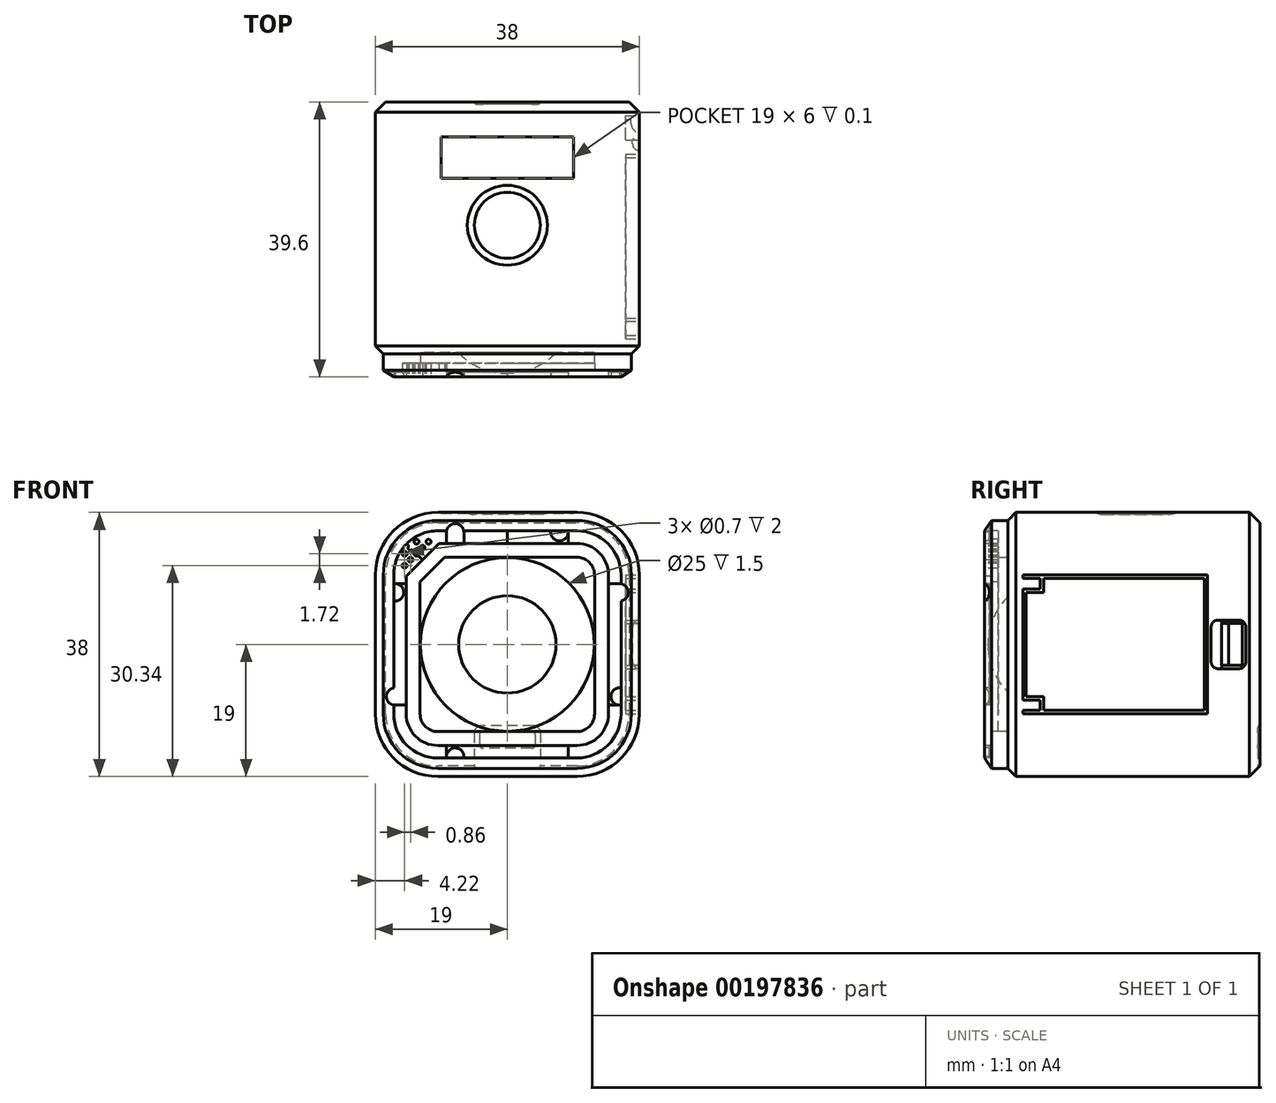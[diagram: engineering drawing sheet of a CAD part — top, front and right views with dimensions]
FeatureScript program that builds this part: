
annotation { "Feature Type Name" : "Feature", "Feature Type Description" : "" }
export const myFeature = defineFeature(function(context is Context, id is Id, definition is map)
    precondition{}
    {
        {
            var Q0;
            Q0=qCreatedBy(makeId("Front.planeOp"),FACE);
            var sketch = newSketch(context, id + "F0", { "sketchPlane" : qUnion([Q0])});
            skLineSegment(sketch, "E0.bottom", {"start": v(19, 19) * mm, "end": v(-19, 19) * mm});
            skLineSegment(sketch, "E0.top", {"start": v(19, -19) * mm, "end": v(-19, -19) * mm});
            skLineSegment(sketch, "E0.left", {"start": v(19, 19) * mm, "end": v(19, -19) * mm});
            skLineSegment(sketch, "E0.right", {"start": v(-19, 19) * mm, "end": v(-19, -19) * mm});
            skPoint(sketch, "E0.middle", {"position": v(0, 0) * mm});
            skLineSegment(sketch, "E1.0", {"start": v(17.85, 17.85) * mm, "end": v(-17.85, 17.85) * mm});
            skLineSegment(sketch, "E1.1", {"start": v(17.85, 17.85) * mm, "end": v(17.85, -17.85) * mm});
            skLineSegment(sketch, "E1.2", {"start": v(17.85, -17.85) * mm, "end": v(-17.85, -17.85) * mm});
            skLineSegment(sketch, "E1.3", {"start": v(-17.85, 17.85) * mm, "end": v(-17.85, -17.85) * mm});
            skSolve(sketch);
        }
        {
            var Q0;
            Q0=makeQuery(id+"F0.imprint","IMPRINT",FACE,{"disambiguationData":[TD([[makeQuery(id+"F0.imprint","IMPRINT",EDGE,{"derivedFrom":sQuery(id+"F0.wireOp",EDGE,"E0.bottom")}),1.0]])]});
            var Q1;
            Q1=makeQuery(id+"F0.imprint","IMPRINT",FACE,{"disambiguationData":[TD([[makeQuery(id+"F0.imprint","IMPRINT",EDGE,{"derivedFrom":sQuery(id+"F0.wireOp",EDGE,"E1.0")}),1.0]])]});
            extrude(context, id + "F1", {"entities" : qUnion([Q0, Q1]), "oppositeDirection" : true, "depth" : 36.6 * mm});
        }
        {
            var Q0;
            Q0=makeQuery(id+"F1.opExtrude","SWEPT_EDGE",EDGE,{"disambiguationData":[OSD([sQuery(id+"F0.wireOp",EDGE,"E0.bottom"),sQuery(id+"F0.wireOp",EDGE,"E0.left")])]});
            var Q1;
            Q1=makeQuery(id+"F1.opExtrude","SWEPT_EDGE",EDGE,{"disambiguationData":[OSD([sQuery(id+"F0.wireOp",EDGE,"E0.bottom"),sQuery(id+"F0.wireOp",EDGE,"E0.right")])]});
            var Q2;
            Q2=makeQuery(id+"F1.opExtrude","SWEPT_EDGE",EDGE,{"disambiguationData":[OSD([sQuery(id+"F0.wireOp",EDGE,"E0.top"),sQuery(id+"F0.wireOp",EDGE,"E0.left")])]});
            var Q3;
            Q3=makeQuery(id+"F1.opExtrude","SWEPT_EDGE",EDGE,{"disambiguationData":[OSD([sQuery(id+"F0.wireOp",EDGE,"E0.top"),sQuery(id+"F0.wireOp",EDGE,"E0.right")])]});
            fillet(context, id + "F2", {"entities" : qUnion([Q0, Q1, Q2, Q3]), "radius" : 9 * mm, "tangentPropagation" : true, "allowEdgeOverflow" : false});
        }
        {
            var Q0;
            Q0=makeQuery(id+"F0.imprint","IMPRINT",FACE,{"disambiguationData":[TD([[makeQuery(id+"F0.imprint","IMPRINT",EDGE,{"derivedFrom":sQuery(id+"F0.wireOp",EDGE,"E1.0")}),1.0]])]});
            extrude(context, id + "F3", {"entities" : qUnion([Q0]), "operationType" : NewBodyOperationType.ADD, "depth" : 3 * mm});
        }
        {
            var Q0;
            Q0=makeQuery(id+"F3.opExtrude","SWEPT_EDGE",EDGE,{"disambiguationData":[OSD([sQuery(id+"F0.wireOp",EDGE,"E1.0"),sQuery(id+"F0.wireOp",EDGE,"E1.1")])]});
            var Q1;
            Q1=makeQuery(id+"F3.opExtrude","SWEPT_EDGE",EDGE,{"disambiguationData":[OSD([sQuery(id+"F0.wireOp",EDGE,"E1.0"),sQuery(id+"F0.wireOp",EDGE,"E1.3")])]});
            var Q2;
            Q2=makeQuery(id+"F3.opExtrude","SWEPT_EDGE",EDGE,{"disambiguationData":[OSD([sQuery(id+"F0.wireOp",EDGE,"E1.2"),sQuery(id+"F0.wireOp",EDGE,"E1.3")])]});
            var Q3;
            Q3=makeQuery(id+"F3.opExtrude","SWEPT_EDGE",EDGE,{"disambiguationData":[OSD([sQuery(id+"F0.wireOp",EDGE,"E1.1"),sQuery(id+"F0.wireOp",EDGE,"E1.2")])]});
            fillet(context, id + "F4", {"entities" : qUnion([Q0, Q1, Q2, Q3]), "radius" : 7.85 * mm, "tangentPropagation" : true, "allowEdgeOverflow" : false});
        }
        {
            var Q0;
            Q0=makeQuery(id+"F1.opExtrude","SWEPT_FACE",FACE,{"disambiguationData":[OSD([sQuery(id+"F0.wireOp",EDGE,"E0.bottom")])]});
            var sketch = newSketch(context, id + "F5", { "sketchPlane" : qUnion([Q0])});
            skCircle(sketch, "E2", {"center": v(0, 18.85) * mm, "radius": 5.75 * mm});
            skCircle(sketch, "E3.0", {"center": v(0, 18.85) * mm, "radius": 4.75 * mm});
            skLineSegment(sketch, "E4.bottom", {"start": v(-9.5, 31.6) * mm, "end": v(9.5, 31.6) * mm});
            skLineSegment(sketch, "E4.top", {"start": v(-9.5, 25.6) * mm, "end": v(9.5, 25.6) * mm});
            skLineSegment(sketch, "E4.left", {"start": v(-9.5, 31.6) * mm, "end": v(-9.5, 25.6) * mm});
            skLineSegment(sketch, "E4.right", {"start": v(9.5, 31.6) * mm, "end": v(9.5, 25.6) * mm});
            skPoint(sketch, "E4.middle", {"position": v(0, 28.6) * mm});
            skSolve(sketch);
        }
        {
            var Q0;
            Q0=makeQuery(id+"F5.imprint","IMPRINT",FACE,{"disambiguationData":[TD([[makeQuery(id+"F5.imprint","IMPRINT",EDGE,{"derivedFrom":sQuery(id+"F5.wireOp",EDGE,"E2")}),1.0]])]});
            extrude(context, id + "F6", {"entities" : qUnion([Q0]), "operationType" : NewBodyOperationType.REMOVE, "oppositeDirection" : true, "depth" : 0.3 * mm});
        }
        {
            var Q0;
            Q0=makeQuery(id+"F6.boolean.opBoolean","COPY",EDGE,{"derivedFrom":makeQuery(id+"F6.opExtrude","CAP_EDGE",EDGE,{"disambiguationData":[OSD([sQuery(id+"F5.wireOp",EDGE,"E3.0")])],"isStart":true})});
            fillet(context, id + "F7", {"entities" : qUnion([Q0]), "radius" : 0.1 * mm, "tangentPropagation" : true, "allowEdgeOverflow" : false});
        }
        {
            var Q0;
            Q0=makeQuery(id+"F5.imprint","IMPRINT",FACE,{"disambiguationData":[TD([[makeQuery(id+"F5.imprint","IMPRINT",EDGE,{"derivedFrom":sQuery(id+"F5.wireOp",EDGE,"E4.bottom")}),-1.0]])]});
            extrude(context, id + "F8", {"entities" : qUnion([Q0]), "operationType" : NewBodyOperationType.REMOVE, "oppositeDirection" : true, "depth" : 0.1 * mm});
        }
        {
            var Q0;
            Q0=makeQuery(id+"F6.boolean.opBoolean","COPY",EDGE,{"derivedFrom":makeQuery(id+"F6.opExtrude","CAP_EDGE",EDGE,{"disambiguationData":[OSD([sQuery(id+"F5.wireOp",EDGE,"E2")])],"isStart":false})});
            fillet(context, id + "F9", {"entities" : qUnion([Q0]), "radius" : 1.7 * mm, "tangentPropagation" : true, "allowEdgeOverflow" : false});
        }
        {
            var Q0;
            Q0=makeQuery(id+"F1.opExtrude","CAP_FACE",FACE,{"disambiguationData":[OSD([sQuery(id+"F0.wireOp",EDGE,"E0.bottom"),sQuery(id+"F0.wireOp",EDGE,"E0.top"),sQuery(id+"F0.wireOp",EDGE,"E0.left"),sQuery(id+"F0.wireOp",EDGE,"E0.right")])],"isStart":false});
            var Q1;
            Q1=makeQuery(id+"F1.opExtrude","CAP_EDGE",EDGE,{"disambiguationData":[OSD([sQuery(id+"F0.wireOp",EDGE,"E0.bottom")])],"isStart":true});
            chamfer(context, id + "F10", {"entities" : qUnion([Q0, Q1]), "width" : 1.5 * mm, "tangentPropagation" : true});
        }
        {
            var Q0;
            Q0=makeQuery(id+"F3.opExtrude","CAP_FACE",FACE,{"disambiguationData":[OSD([sQuery(id+"F0.wireOp",EDGE,"E1.0"),sQuery(id+"F0.wireOp",EDGE,"E1.1"),sQuery(id+"F0.wireOp",EDGE,"E1.2"),sQuery(id+"F0.wireOp",EDGE,"E1.3")])],"isStart":false});
            chamfer(context, id + "F11", {"entities" : qUnion([Q0]), "chamferType" : ChamferType.TWO_OFFSETS, "width1" : 1.5 * mm, "oppositeDirection" : false, "width2" : 1 * mm, "tangentPropagation" : true});
        }
        {
            var Q0;
            Q0=makeQuery(id+"F3.opExtrude","CAP_FACE",FACE,{"disambiguationData":[OSD([sQuery(id+"F0.wireOp",EDGE,"E1.0"),sQuery(id+"F0.wireOp",EDGE,"E1.1"),sQuery(id+"F0.wireOp",EDGE,"E1.2"),sQuery(id+"F0.wireOp",EDGE,"E1.3")])],"isStart":false});
            var sketch = newSketch(context, id + "F12", { "sketchPlane" : qUnion([Q0])});
            skLineSegment(sketch, "E5.1", {"start": v(10, 14.55) * mm, "end": v(-9.85, 14.55) * mm});
            skLineSegment(sketch, "E5.2", {"start": v(-14.55, 9.85) * mm, "end": v(-14.55, -10) * mm});
            skArc(sketch, "E5.3", {"start": v(14.55, 10) * mm, "mid": v(13.22, 13.22) * mm, "end": v(10, 14.55) * mm});
            skArc(sketch, "E5.4", {"start": v(-14.55, -10) * mm, "mid": v(-13.22, -13.22) * mm, "end": v(-10, -14.55) * mm});
            skLineSegment(sketch, "E5.5", {"start": v(-10, -14.55) * mm, "end": v(10, -14.55) * mm});
            skArc(sketch, "E5.6", {"start": v(10, -14.55) * mm, "mid": v(13.22, -13.22) * mm, "end": v(14.55, -10) * mm});
            skLineSegment(sketch, "E5.7", {"start": v(14.55, -10) * mm, "end": v(14.55, 10) * mm});
            skLineSegment(sketch, "E6", {"start": v(-14.55, 9.85) * mm, "end": v(-9.85, 14.55) * mm});
            skCircle(sketch, "E7", {"center": v(-13.06, 13.06) * mm, "radius": 0.35 * mm});
            skLineSegment(sketch, "E8", {"start": v(-12.2, 12.2) * mm, "end": v(-14.5, 14.5) * mm});
            skCircle(sketch, "E9", {"center": v(-13.92, 13.92) * mm, "radius": 0.35 * mm});
            skCircle(sketch, "E10", {"center": v(-13.92, 12.2) * mm, "radius": 0.35 * mm});
            skCircle(sketch, "E11", {"center": v(-14.78, 11.34) * mm, "radius": 0.35 * mm});
            skCircle(sketch, "E12", {"center": v(-14.78, 13.06) * mm, "radius": 0.35 * mm});
            skCircle(sketch, "E13.MirrorC", {"center": v(-12.2, 13.92) * mm, "radius": 0.35 * mm});
            skCircle(sketch, "E14.MirrorC", {"center": v(-13.06, 14.78) * mm, "radius": 0.35 * mm});
            skCircle(sketch, "E15.MirrorC", {"center": v(-11.34, 14.78) * mm, "radius": 0.35 * mm});
            skPoint(sketch, "E16", {"position": v(-7.5, 16.15) * mm});
            skLineSegment(sketch, "E17", {"start": v(0, 16.35) * mm, "end": v(0, 14.55) * mm});
            skCircle(sketch, "E18", {"center": v(-7.5, 16.15) * mm, "radius": 1.25 * mm});
            skLineSegment(sketch, "E19", {"start": v(-8.75, 16.15) * mm, "end": v(-8.75, 14.55) * mm});
            skLineSegment(sketch, "E20", {"start": v(-6.25, 16.15) * mm, "end": v(-6.25, 14.55) * mm});
            skLineSegment(sketch, "E21.MirrorCS", {"start": v(6.25, 16.15) * mm, "end": v(6.25, 14.55) * mm});
            skCircle(sketch, "E22.MirrorC", {"center": v(7.5, 16.15) * mm, "radius": 1.25 * mm});
            skLineSegment(sketch, "E23.MirrorCS", {"start": v(8.75, 16.15) * mm, "end": v(8.75, 14.55) * mm});
            skLineSegment(sketch, "E24.MirrorCS", {"start": v(-6.25, -16.15) * mm, "end": v(-6.25, -14.55) * mm});
            skCircle(sketch, "E25.MirrorC", {"center": v(-7.5, -16.15) * mm, "radius": 1.25 * mm});
            skLineSegment(sketch, "E26.MirrorCS", {"start": v(-8.75, -16.15) * mm, "end": v(-8.75, -14.55) * mm});
            skLineSegment(sketch, "E27.MirrorCS", {"start": v(6.25, -16.15) * mm, "end": v(6.25, -14.55) * mm});
            skCircle(sketch, "E28.MirrorC", {"center": v(7.5, -16.15) * mm, "radius": 1.25 * mm});
            skLineSegment(sketch, "E29.MirrorCS", {"start": v(8.75, -16.15) * mm, "end": v(8.75, -14.55) * mm});
            skLineSegment(sketch, "E30.MirrorCS", {"start": v(-16.15, -8.75) * mm, "end": v(-14.55, -8.75) * mm});
            skCircle(sketch, "E31.MirrorC", {"center": v(-16.15, -7.5) * mm, "radius": 1.25 * mm});
            skLineSegment(sketch, "E32.MirrorCS", {"start": v(-16.15, -6.25) * mm, "end": v(-14.55, -6.25) * mm});
            skLineSegment(sketch, "E33.MirrorCS", {"start": v(-16.15, 6.25) * mm, "end": v(-14.55, 6.25) * mm});
            skCircle(sketch, "E34.MirrorC", {"center": v(-16.15, 7.5) * mm, "radius": 1.25 * mm});
            skLineSegment(sketch, "E35.MirrorCS", {"start": v(-16.15, 8.75) * mm, "end": v(-14.55, 8.75) * mm});
            skLineSegment(sketch, "E36.MirrorCS", {"start": v(16.15, 8.75) * mm, "end": v(14.55, 8.75) * mm});
            skCircle(sketch, "E37.MirrorC", {"center": v(16.15, 7.5) * mm, "radius": 1.25 * mm});
            skLineSegment(sketch, "E38.MirrorCS", {"start": v(16.15, 6.25) * mm, "end": v(14.55, 6.25) * mm});
            skLineSegment(sketch, "E39.MirrorCS", {"start": v(16.15, -6.25) * mm, "end": v(14.55, -6.25) * mm});
            skCircle(sketch, "E40.MirrorC", {"center": v(16.15, -7.5) * mm, "radius": 1.25 * mm});
            skLineSegment(sketch, "E41.MirrorCS", {"start": v(16.15, -8.75) * mm, "end": v(14.55, -8.75) * mm});
            skSolve(sketch);
        }
        {
            var Q0;
            Q0=makeQuery(id+"F12.imprint","IMPRINT",FACE,{"disambiguationData":[TD([[makeQuery(id+"F12.imprint","IMPRINT",EDGE,{"derivedFrom":sQuery(id+"F12.wireOp",EDGE,"E5.1")}),1.0]])]});
            extrude(context, id + "F13", {"entities" : qUnion([Q0]), "operationType" : NewBodyOperationType.REMOVE, "oppositeDirection" : true, "depth" : 1 * mm});
        }
        {
            var Q0;
            Q0=makeQuery(id+"F13.boolean.opBoolean","COPY",FACE,{"derivedFrom":makeQuery(id+"F13.opExtrude","CAP_FACE",FACE,{"disambiguationData":[OSD([sQuery(id+"F12.wireOp",EDGE,"E5.1"),sQuery(id+"F12.wireOp",EDGE,"E5.2"),sQuery(id+"F12.wireOp",EDGE,"E5.3"),sQuery(id+"F12.wireOp",EDGE,"E5.4"),sQuery(id+"F12.wireOp",EDGE,"E5.5"),sQuery(id+"F12.wireOp",EDGE,"E5.6"),sQuery(id+"F12.wireOp",EDGE,"E5.7"),sQuery(id+"F12.wireOp",EDGE,"E6")])],"isStart":false})});
            var sketch = newSketch(context, id + "F14", { "sketchPlane" : qUnion([Q0])});
            skLineSegment(sketch, "E42.0", {"start": v(12.55, -10) * mm, "end": v(12.55, 10) * mm});
            skArc(sketch, "E42.1", {"start": v(10, -12.55) * mm, "mid": v(11.8, -11.8) * mm, "end": v(12.55, -10) * mm});
            skArc(sketch, "E42.2", {"start": v(12.55, 10) * mm, "mid": v(11.8, 11.8) * mm, "end": v(10, 12.55) * mm});
            skLineSegment(sketch, "E42.3", {"start": v(-10, -12.55) * mm, "end": v(10, -12.55) * mm});
            skLineSegment(sketch, "E42.4", {"start": v(10, 12.55) * mm, "end": v(-9.02, 12.55) * mm});
            skLineSegment(sketch, "E42.5", {"start": v(-9.02, 12.55) * mm, "end": v(-12.55, 9.02) * mm});
            skLineSegment(sketch, "E42.6", {"start": v(-12.55, 9.02) * mm, "end": v(-12.55, -10) * mm});
            skArc(sketch, "E42.7", {"start": v(-12.55, -10) * mm, "mid": v(-11.8, -11.8) * mm, "end": v(-10, -12.55) * mm});
            skCircle(sketch, "E43", {"center": v(0, 0) * mm, "radius": 12.5 * mm});
            skPoint(sketch, "E44", {"position": v(0, -12.55) * mm});
            skPoint(sketch, "E45", {"position": v(12.55, 0) * mm});
            skSolve(sketch);
        }
        {
            var Q0;
            Q0=makeQuery(id+"F14.imprint","IMPRINT",FACE,{"disambiguationData":[TD([[makeQuery(id+"F14.imprint","IMPRINT",EDGE,{"derivedFrom":sQuery(id+"F14.wireOp",EDGE,"E42.0")}),1.0]])]});
            extrude(context, id + "F15", {"entities" : qUnion([Q0]), "operationType" : NewBodyOperationType.REMOVE, "oppositeDirection" : true, "depth" : 1 * mm});
        }
        {
            var Q0;
            Q0=makeQuery(id+"F15.boolean.opBoolean","SPLIT",FACE,{"disambiguationData":[TD([makeQuery(id+"F15.opExtrude","SWEPT_FACE",FACE,{"disambiguationData":[OSD([sQuery(id+"F14.wireOp",EDGE,"E43")])]})])],"derivedFrom":makeQuery(id+"F13.boolean.opBoolean","COPY",FACE,{"derivedFrom":makeQuery(id+"F13.opExtrude","CAP_FACE",FACE,{"disambiguationData":[OSD([sQuery(id+"F12.wireOp",EDGE,"E5.1"),sQuery(id+"F12.wireOp",EDGE,"E5.2"),sQuery(id+"F12.wireOp",EDGE,"E5.3"),sQuery(id+"F12.wireOp",EDGE,"E5.4"),sQuery(id+"F12.wireOp",EDGE,"E5.5"),sQuery(id+"F12.wireOp",EDGE,"E5.6"),sQuery(id+"F12.wireOp",EDGE,"E5.7"),sQuery(id+"F12.wireOp",EDGE,"E6")])],"isStart":false})})});
            extrude(context, id + "F16", {"entities" : qUnion([Q0]), "operationType" : NewBodyOperationType.REMOVE, "oppositeDirection" : true, "depth" : 2.5 * mm});
        }
        {
            var Q0;
            Q0=makeQuery(id+"F16.boolean.opBoolean","COPY",FACE,{"derivedFrom":makeQuery(id+"F16.opExtrude","CAP_FACE",FACE,{"disambiguationData":[OSD([sQuery(id+"F12.wireOp",EDGE,"E5.1"),sQuery(id+"F12.wireOp",EDGE,"E5.2"),sQuery(id+"F12.wireOp",EDGE,"E5.3"),sQuery(id+"F12.wireOp",EDGE,"E5.4"),sQuery(id+"F12.wireOp",EDGE,"E5.5"),sQuery(id+"F12.wireOp",EDGE,"E5.6"),sQuery(id+"F12.wireOp",EDGE,"E5.7"),sQuery(id+"F12.wireOp",EDGE,"E6")])],"isStart":false})});
            var sketch = newSketch(context, id + "F17", { "sketchPlane" : qUnion([Q0])});
            skCircle(sketch, "E46.0", {"center": v(0, 0) * mm, "radius": 7 * mm});
            skCircle(sketch, "E47.0", {"center": v(0, 0) * mm, "radius": 17.5 * mm});
            skSolve(sketch);
        }
        {
            var Q0;
            Q0=makeQuery(id+"F17.imprint","IMPRINT",FACE,{"disambiguationData":[TD([[makeQuery(id+"F17.imprint","IMPRINT",EDGE,{"derivedFrom":sQuery(id+"F17.wireOp",EDGE,"E46.0")}),1.0]])]});
            extrude(context, id + "F18", {"entities" : qUnion([Q0]), "operationType" : NewBodyOperationType.ADD, "depth" : 3 * mm});
        }
        {
            var Q0;
            Q0=makeQuery(id+"F18.opExtrude","CAP_EDGE",EDGE,{"disambiguationData":[OSD([sQuery(id+"F17.wireOp",EDGE,"E46.0")])],"isStart":false});
            fillet(context, id + "F19", {"entities" : qUnion([Q0]), "radius" : 9.5 * mm, "tangentPropagation" : true, "allowEdgeOverflow" : false});
        }
        {
            var Q0;
            Q0=makeQuery(id+"F12.imprint","IMPRINT",FACE,{"disambiguationData":[TD([[makeQuery(id+"F12.imprint","IMPRINT",EDGE,{"derivedFrom":sQuery(id+"F12.wireOp",EDGE,"E11")}),1.0]])]});
            var Q1;
            Q1=makeQuery(id+"F12.imprint","IMPRINT",FACE,{"disambiguationData":[TD([[makeQuery(id+"F12.imprint","IMPRINT",EDGE,{"derivedFrom":sQuery(id+"F12.wireOp",EDGE,"E10")}),1.0]])]});
            var Q2;
            Q2=makeQuery(id+"F12.imprint","IMPRINT",FACE,{"disambiguationData":[TD([[makeQuery(id+"F12.imprint","IMPRINT",EDGE,{"derivedFrom":sQuery(id+"F12.wireOp",EDGE,"E12")}),1.0]])]});
            var Q3;
            {var subQ0=sQuery(id+"F12.wireOp",EDGE,"E9");var subQ1=sQuery(id+"F12.wireOp",EDGE,"E8");var subQ2=makeQuery(id+"F12.imprint","INTERSECT",VERTEX,{"disambiguationData":[OD(0.0)],"derivedFrom":[subQ1,subQ0]});Q3=makeQuery(id+"F12.imprint","IMPRINT",FACE,{"disambiguationData":[TD([[makeQuery(id+"F12.imprint","IMPRINT",EDGE,{"disambiguationData":[TD([[subQ2,-1.0]])],"derivedFrom":subQ1}),1.0]])]});}
            var Q4;
            {var subQ0=sQuery(id+"F12.wireOp",EDGE,"E9");var subQ1=sQuery(id+"F12.wireOp",EDGE,"E8");var subQ2=makeQuery(id+"F12.imprint","INTERSECT",VERTEX,{"disambiguationData":[OD(0.0)],"derivedFrom":[subQ1,subQ0]});Q4=makeQuery(id+"F12.imprint","IMPRINT",FACE,{"disambiguationData":[TD([[makeQuery(id+"F12.imprint","IMPRINT",EDGE,{"disambiguationData":[TD([[subQ2,-1.0]])],"derivedFrom":subQ1}),-1.0]])]});}
            var Q5;
            Q5=makeQuery(id+"F12.imprint","IMPRINT",FACE,{"disambiguationData":[TD([[makeQuery(id+"F12.imprint","IMPRINT",EDGE,{"derivedFrom":sQuery(id+"F12.wireOp",EDGE,"E14.MirrorC")}),-1.0]])]});
            var Q6;
            {var subQ0=sQuery(id+"F12.wireOp",EDGE,"E8");var subQ1=sQuery(id+"F12.wireOp",EDGE,"E7");var subQ2=makeQuery(id+"F12.imprint","INTERSECT",VERTEX,{"disambiguationData":[OD(0.0)],"derivedFrom":[subQ1,subQ0]});Q6=makeQuery(id+"F12.imprint","IMPRINT",FACE,{"disambiguationData":[TD([[makeQuery(id+"F12.imprint","IMPRINT",EDGE,{"disambiguationData":[TD([[subQ2,1.0]])],"derivedFrom":subQ1}),1.0]])]});}
            var Q7;
            {var subQ0=sQuery(id+"F12.wireOp",EDGE,"E8");var subQ1=sQuery(id+"F12.wireOp",EDGE,"E7");var subQ2=makeQuery(id+"F12.imprint","INTERSECT",VERTEX,{"disambiguationData":[OD(0.0)],"derivedFrom":[subQ1,subQ0]});Q7=makeQuery(id+"F12.imprint","IMPRINT",FACE,{"disambiguationData":[TD([[makeQuery(id+"F12.imprint","IMPRINT",EDGE,{"disambiguationData":[TD([[subQ2,-1.0]])],"derivedFrom":subQ1}),1.0]])]});}
            var Q8;
            Q8=makeQuery(id+"F12.imprint","IMPRINT",FACE,{"disambiguationData":[TD([[makeQuery(id+"F12.imprint","IMPRINT",EDGE,{"derivedFrom":sQuery(id+"F12.wireOp",EDGE,"E15.MirrorC")}),-1.0]])]});
            var Q9;
            Q9=makeQuery(id+"F12.imprint","IMPRINT",FACE,{"disambiguationData":[TD([[makeQuery(id+"F12.imprint","IMPRINT",EDGE,{"derivedFrom":sQuery(id+"F12.wireOp",EDGE,"E13.MirrorC")}),-1.0]])]});
            extrude(context, id + "F20", {"entities" : qUnion([Q0, Q1, Q2, Q3, Q4, Q5, Q6, Q7, Q8, Q9]), "operationType" : NewBodyOperationType.REMOVE, "oppositeDirection" : true, "depth" : 2 * mm});
        }
        {
            var Q0;
            {var subQ0=sQuery(id+"F12.wireOp",EDGE,"E18");var subQ1=sQuery(id+"F0.wireOp",EDGE,"E1.0");var subQ2=makeQuery(id+"F11.opChamfer","BLEND_EDGE",EDGE,{"blendedFrom":[makeQuery(id+"F3.opExtrude","CAP_EDGE",EDGE,{"disambiguationData":[OSD([subQ1])],"isStart":false}),makeQuery(id+"F3.opExtrude","CAP_FACE",FACE,{"disambiguationData":[OSD([subQ1,sQuery(id+"F0.wireOp",EDGE,"E1.1"),sQuery(id+"F0.wireOp",EDGE,"E1.2"),sQuery(id+"F0.wireOp",EDGE,"E1.3")])],"isStart":false})],"blendedInto":[makeQuery(id+"F3.opExtrude","CAP_FACE",FACE,{"disambiguationData":[OSD([subQ1,sQuery(id+"F0.wireOp",EDGE,"E1.1"),sQuery(id+"F0.wireOp",EDGE,"E1.2"),sQuery(id+"F0.wireOp",EDGE,"E1.3")])],"isStart":false})]});var subQ3=makeQuery(id+"F12.imprint","INTERSECT",VERTEX,{"disambiguationData":[OD(0.0)],"derivedFrom":[subQ2,subQ0]});Q0=makeQuery(id+"F12.imprint","IMPRINT",FACE,{"disambiguationData":[TD([[makeQuery(id+"F12.imprint","IMPRINT",EDGE,{"disambiguationData":[TD([[subQ3,-1.0]])],"derivedFrom":subQ0}),1.0]])]});}
            var Q1;
            {var subQ0=sQuery(id+"F12.wireOp",EDGE,"E18");var subQ5=makeQuery(id+"F12.imprint","INTERSECT",VERTEX,{"derivedFrom":[subQ0,sQuery(id+"F12.wireOp",EDGE,"E19")]});Q1=makeQuery(id+"F12.imprint","IMPRINT",FACE,{"disambiguationData":[TD([[makeQuery(id+"F12.imprint","IMPRINT",EDGE,{"disambiguationData":[TD([[subQ5,-1.0]])],"derivedFrom":subQ0}),1.0]])]});}
            var Q2;
            {var subQ0=sQuery(id+"F12.wireOp",EDGE,"E19");Q2=makeQuery(id+"F12.imprint","IMPRINT",FACE,{"disambiguationData":[TD([[makeQuery(id+"F12.imprint","IMPRINT",EDGE,{"derivedFrom":subQ0}),1.0]])]});}
            var Q3;
            {var subQ0=sQuery(id+"F12.wireOp",EDGE,"E22.MirrorC");var subQ1=sQuery(id+"F0.wireOp",EDGE,"E1.0");var subQ2=makeQuery(id+"F11.opChamfer","BLEND_EDGE",EDGE,{"blendedFrom":[makeQuery(id+"F3.opExtrude","CAP_EDGE",EDGE,{"disambiguationData":[OSD([subQ1])],"isStart":false}),makeQuery(id+"F3.opExtrude","CAP_FACE",FACE,{"disambiguationData":[OSD([subQ1,sQuery(id+"F0.wireOp",EDGE,"E1.1"),sQuery(id+"F0.wireOp",EDGE,"E1.2"),sQuery(id+"F0.wireOp",EDGE,"E1.3")])],"isStart":false})],"blendedInto":[makeQuery(id+"F3.opExtrude","CAP_FACE",FACE,{"disambiguationData":[OSD([subQ1,sQuery(id+"F0.wireOp",EDGE,"E1.1"),sQuery(id+"F0.wireOp",EDGE,"E1.2"),sQuery(id+"F0.wireOp",EDGE,"E1.3")])],"isStart":false})]});var subQ3=makeQuery(id+"F12.imprint","INTERSECT",VERTEX,{"disambiguationData":[OD(0.0)],"derivedFrom":[subQ2,subQ0]});Q3=makeQuery(id+"F12.imprint","IMPRINT",FACE,{"disambiguationData":[TD([[makeQuery(id+"F12.imprint","IMPRINT",EDGE,{"disambiguationData":[TD([[subQ3,-1.0]])],"derivedFrom":subQ0}),-1.0]])]});}
            var Q4;
            {var subQ0=sQuery(id+"F12.wireOp",EDGE,"E22.MirrorC");var subQ1=makeQuery(id+"F12.imprint","INTERSECT",VERTEX,{"derivedFrom":[sQuery(id+"F12.wireOp",EDGE,"E21.MirrorCS"),subQ0]});Q4=makeQuery(id+"F12.imprint","IMPRINT",FACE,{"disambiguationData":[TD([[makeQuery(id+"F12.imprint","IMPRINT",EDGE,{"disambiguationData":[TD([[subQ1,1.0]])],"derivedFrom":subQ0}),-1.0]])]});}
            var Q5;
            {var subQ0=sQuery(id+"F12.wireOp",EDGE,"E21.MirrorCS");Q5=makeQuery(id+"F12.imprint","IMPRINT",FACE,{"disambiguationData":[TD([[makeQuery(id+"F12.imprint","IMPRINT",EDGE,{"derivedFrom":subQ0}),1.0]])]});}
            var Q6;
            {var subQ0=sQuery(id+"F12.wireOp",EDGE,"E36.MirrorCS");Q6=makeQuery(id+"F12.imprint","IMPRINT",FACE,{"disambiguationData":[TD([[makeQuery(id+"F12.imprint","IMPRINT",EDGE,{"derivedFrom":subQ0}),1.0]])]});}
            var Q7;
            {var subQ0=sQuery(id+"F12.wireOp",EDGE,"E37.MirrorC");var subQ5=makeQuery(id+"F12.imprint","INTERSECT",VERTEX,{"derivedFrom":[sQuery(id+"F12.wireOp",EDGE,"E36.MirrorCS"),subQ0]});Q7=makeQuery(id+"F12.imprint","IMPRINT",FACE,{"disambiguationData":[TD([[makeQuery(id+"F12.imprint","IMPRINT",EDGE,{"disambiguationData":[TD([[subQ5,-1.0]])],"derivedFrom":subQ0}),1.0]])]});}
            var Q8;
            {var subQ0=sQuery(id+"F12.wireOp",EDGE,"E37.MirrorC");var subQ1=sQuery(id+"F0.wireOp",EDGE,"E1.1");var subQ2=makeQuery(id+"F11.opChamfer","BLEND_EDGE",EDGE,{"blendedFrom":[makeQuery(id+"F3.opExtrude","CAP_EDGE",EDGE,{"disambiguationData":[OSD([subQ1])],"isStart":false}),makeQuery(id+"F3.opExtrude","CAP_FACE",FACE,{"disambiguationData":[OSD([sQuery(id+"F0.wireOp",EDGE,"E1.0"),subQ1,sQuery(id+"F0.wireOp",EDGE,"E1.2"),sQuery(id+"F0.wireOp",EDGE,"E1.3")])],"isStart":false})],"blendedInto":[makeQuery(id+"F3.opExtrude","CAP_FACE",FACE,{"disambiguationData":[OSD([sQuery(id+"F0.wireOp",EDGE,"E1.0"),subQ1,sQuery(id+"F0.wireOp",EDGE,"E1.2"),sQuery(id+"F0.wireOp",EDGE,"E1.3")])],"isStart":false})]});var subQ3=makeQuery(id+"F12.imprint","INTERSECT",VERTEX,{"disambiguationData":[OD(0.0)],"derivedFrom":[subQ2,subQ0]});Q8=makeQuery(id+"F12.imprint","IMPRINT",FACE,{"disambiguationData":[TD([[makeQuery(id+"F12.imprint","IMPRINT",EDGE,{"disambiguationData":[TD([[subQ3,-1.0]])],"derivedFrom":subQ0}),1.0]])]});}
            var Q9;
            {var subQ0=sQuery(id+"F12.wireOp",EDGE,"E39.MirrorCS");Q9=makeQuery(id+"F12.imprint","IMPRINT",FACE,{"disambiguationData":[TD([[makeQuery(id+"F12.imprint","IMPRINT",EDGE,{"derivedFrom":subQ0}),1.0]])]});}
            var Q10;
            {var subQ0=sQuery(id+"F12.wireOp",EDGE,"E40.MirrorC");var subQ1=makeQuery(id+"F12.imprint","INTERSECT",VERTEX,{"derivedFrom":[sQuery(id+"F12.wireOp",EDGE,"E39.MirrorCS"),subQ0]});Q10=makeQuery(id+"F12.imprint","IMPRINT",FACE,{"disambiguationData":[TD([[makeQuery(id+"F12.imprint","IMPRINT",EDGE,{"disambiguationData":[TD([[subQ1,1.0]])],"derivedFrom":subQ0}),-1.0]])]});}
            var Q11;
            {var subQ0=sQuery(id+"F12.wireOp",EDGE,"E40.MirrorC");var subQ1=sQuery(id+"F0.wireOp",EDGE,"E1.1");var subQ2=makeQuery(id+"F11.opChamfer","BLEND_EDGE",EDGE,{"blendedFrom":[makeQuery(id+"F3.opExtrude","CAP_EDGE",EDGE,{"disambiguationData":[OSD([subQ1])],"isStart":false}),makeQuery(id+"F3.opExtrude","CAP_FACE",FACE,{"disambiguationData":[OSD([sQuery(id+"F0.wireOp",EDGE,"E1.0"),subQ1,sQuery(id+"F0.wireOp",EDGE,"E1.2"),sQuery(id+"F0.wireOp",EDGE,"E1.3")])],"isStart":false})],"blendedInto":[makeQuery(id+"F3.opExtrude","CAP_FACE",FACE,{"disambiguationData":[OSD([sQuery(id+"F0.wireOp",EDGE,"E1.0"),subQ1,sQuery(id+"F0.wireOp",EDGE,"E1.2"),sQuery(id+"F0.wireOp",EDGE,"E1.3")])],"isStart":false})]});var subQ3=makeQuery(id+"F12.imprint","INTERSECT",VERTEX,{"disambiguationData":[OD(0.0)],"derivedFrom":[subQ2,subQ0]});Q11=makeQuery(id+"F12.imprint","IMPRINT",FACE,{"disambiguationData":[TD([[makeQuery(id+"F12.imprint","IMPRINT",EDGE,{"disambiguationData":[TD([[subQ3,-1.0]])],"derivedFrom":subQ0}),-1.0]])]});}
            var Q12;
            {var subQ0=sQuery(id+"F12.wireOp",EDGE,"E27.MirrorCS");Q12=makeQuery(id+"F12.imprint","IMPRINT",FACE,{"disambiguationData":[TD([[makeQuery(id+"F12.imprint","IMPRINT",EDGE,{"derivedFrom":subQ0}),-1.0]])]});}
            var Q13;
            {var subQ0=sQuery(id+"F12.wireOp",EDGE,"E28.MirrorC");var subQ1=makeQuery(id+"F12.imprint","INTERSECT",VERTEX,{"derivedFrom":[sQuery(id+"F12.wireOp",EDGE,"E27.MirrorCS"),subQ0]});Q13=makeQuery(id+"F12.imprint","IMPRINT",FACE,{"disambiguationData":[TD([[makeQuery(id+"F12.imprint","IMPRINT",EDGE,{"disambiguationData":[TD([[subQ1,1.0]])],"derivedFrom":subQ0}),1.0]])]});}
            var Q14;
            {var subQ0=sQuery(id+"F12.wireOp",EDGE,"E28.MirrorC");var subQ1=sQuery(id+"F0.wireOp",EDGE,"E1.2");var subQ2=makeQuery(id+"F11.opChamfer","BLEND_EDGE",EDGE,{"blendedFrom":[makeQuery(id+"F3.opExtrude","CAP_EDGE",EDGE,{"disambiguationData":[OSD([subQ1])],"isStart":false}),makeQuery(id+"F3.opExtrude","CAP_FACE",FACE,{"disambiguationData":[OSD([sQuery(id+"F0.wireOp",EDGE,"E1.0"),sQuery(id+"F0.wireOp",EDGE,"E1.1"),subQ1,sQuery(id+"F0.wireOp",EDGE,"E1.3")])],"isStart":false})],"blendedInto":[makeQuery(id+"F3.opExtrude","CAP_FACE",FACE,{"disambiguationData":[OSD([sQuery(id+"F0.wireOp",EDGE,"E1.0"),sQuery(id+"F0.wireOp",EDGE,"E1.1"),subQ1,sQuery(id+"F0.wireOp",EDGE,"E1.3")])],"isStart":false})]});var subQ3=makeQuery(id+"F12.imprint","INTERSECT",VERTEX,{"disambiguationData":[OD(0.0)],"derivedFrom":[subQ2,subQ0]});Q14=makeQuery(id+"F12.imprint","IMPRINT",FACE,{"disambiguationData":[TD([[makeQuery(id+"F12.imprint","IMPRINT",EDGE,{"disambiguationData":[TD([[subQ3,-1.0]])],"derivedFrom":subQ0}),1.0]])]});}
            var Q15;
            {var subQ0=sQuery(id+"F12.wireOp",EDGE,"E24.MirrorCS");Q15=makeQuery(id+"F12.imprint","IMPRINT",FACE,{"disambiguationData":[TD([[makeQuery(id+"F12.imprint","IMPRINT",EDGE,{"derivedFrom":subQ0}),1.0]])]});}
            var Q16;
            {var subQ0=sQuery(id+"F12.wireOp",EDGE,"E25.MirrorC");var subQ1=makeQuery(id+"F12.imprint","INTERSECT",VERTEX,{"derivedFrom":[sQuery(id+"F12.wireOp",EDGE,"E24.MirrorCS"),subQ0]});Q16=makeQuery(id+"F12.imprint","IMPRINT",FACE,{"disambiguationData":[TD([[makeQuery(id+"F12.imprint","IMPRINT",EDGE,{"disambiguationData":[TD([[subQ1,1.0]])],"derivedFrom":subQ0}),-1.0]])]});}
            var Q17;
            {var subQ0=sQuery(id+"F12.wireOp",EDGE,"E25.MirrorC");var subQ1=sQuery(id+"F0.wireOp",EDGE,"E1.2");var subQ2=makeQuery(id+"F11.opChamfer","BLEND_EDGE",EDGE,{"blendedFrom":[makeQuery(id+"F3.opExtrude","CAP_EDGE",EDGE,{"disambiguationData":[OSD([subQ1])],"isStart":false}),makeQuery(id+"F3.opExtrude","CAP_FACE",FACE,{"disambiguationData":[OSD([sQuery(id+"F0.wireOp",EDGE,"E1.0"),sQuery(id+"F0.wireOp",EDGE,"E1.1"),subQ1,sQuery(id+"F0.wireOp",EDGE,"E1.3")])],"isStart":false})],"blendedInto":[makeQuery(id+"F3.opExtrude","CAP_FACE",FACE,{"disambiguationData":[OSD([sQuery(id+"F0.wireOp",EDGE,"E1.0"),sQuery(id+"F0.wireOp",EDGE,"E1.1"),subQ1,sQuery(id+"F0.wireOp",EDGE,"E1.3")])],"isStart":false})]});var subQ3=makeQuery(id+"F12.imprint","INTERSECT",VERTEX,{"disambiguationData":[OD(0.0)],"derivedFrom":[subQ2,subQ0]});Q17=makeQuery(id+"F12.imprint","IMPRINT",FACE,{"disambiguationData":[TD([[makeQuery(id+"F12.imprint","IMPRINT",EDGE,{"disambiguationData":[TD([[subQ3,-1.0]])],"derivedFrom":subQ0}),-1.0]])]});}
            var Q18;
            {var subQ0=sQuery(id+"F12.wireOp",EDGE,"E34.MirrorC");var subQ1=sQuery(id+"F0.wireOp",EDGE,"E1.3");var subQ2=makeQuery(id+"F11.opChamfer","BLEND_EDGE",EDGE,{"blendedFrom":[makeQuery(id+"F3.opExtrude","CAP_EDGE",EDGE,{"disambiguationData":[OSD([subQ1])],"isStart":false}),makeQuery(id+"F3.opExtrude","CAP_FACE",FACE,{"disambiguationData":[OSD([sQuery(id+"F0.wireOp",EDGE,"E1.0"),sQuery(id+"F0.wireOp",EDGE,"E1.1"),sQuery(id+"F0.wireOp",EDGE,"E1.2"),subQ1])],"isStart":false})],"blendedInto":[makeQuery(id+"F3.opExtrude","CAP_FACE",FACE,{"disambiguationData":[OSD([sQuery(id+"F0.wireOp",EDGE,"E1.0"),sQuery(id+"F0.wireOp",EDGE,"E1.1"),sQuery(id+"F0.wireOp",EDGE,"E1.2"),subQ1])],"isStart":false})]});var subQ3=makeQuery(id+"F12.imprint","INTERSECT",VERTEX,{"disambiguationData":[OD(0.0)],"derivedFrom":[subQ2,subQ0]});Q18=makeQuery(id+"F12.imprint","IMPRINT",FACE,{"disambiguationData":[TD([[makeQuery(id+"F12.imprint","IMPRINT",EDGE,{"disambiguationData":[TD([[subQ3,-1.0]])],"derivedFrom":subQ0}),-1.0]])]});}
            var Q19;
            {var subQ0=sQuery(id+"F12.wireOp",EDGE,"E34.MirrorC");var subQ1=makeQuery(id+"F12.imprint","INTERSECT",VERTEX,{"derivedFrom":[sQuery(id+"F12.wireOp",EDGE,"E33.MirrorCS"),subQ0]});Q19=makeQuery(id+"F12.imprint","IMPRINT",FACE,{"disambiguationData":[TD([[makeQuery(id+"F12.imprint","IMPRINT",EDGE,{"disambiguationData":[TD([[subQ1,1.0]])],"derivedFrom":subQ0}),-1.0]])]});}
            var Q20;
            {var subQ0=sQuery(id+"F12.wireOp",EDGE,"E33.MirrorCS");Q20=makeQuery(id+"F12.imprint","IMPRINT",FACE,{"disambiguationData":[TD([[makeQuery(id+"F12.imprint","IMPRINT",EDGE,{"derivedFrom":subQ0}),1.0]])]});}
            var Q21;
            {var subQ0=sQuery(id+"F12.wireOp",EDGE,"E31.MirrorC");var subQ1=sQuery(id+"F0.wireOp",EDGE,"E1.3");var subQ2=makeQuery(id+"F11.opChamfer","BLEND_EDGE",EDGE,{"blendedFrom":[makeQuery(id+"F3.opExtrude","CAP_EDGE",EDGE,{"disambiguationData":[OSD([subQ1])],"isStart":false}),makeQuery(id+"F3.opExtrude","CAP_FACE",FACE,{"disambiguationData":[OSD([sQuery(id+"F0.wireOp",EDGE,"E1.0"),sQuery(id+"F0.wireOp",EDGE,"E1.1"),sQuery(id+"F0.wireOp",EDGE,"E1.2"),subQ1])],"isStart":false})],"blendedInto":[makeQuery(id+"F3.opExtrude","CAP_FACE",FACE,{"disambiguationData":[OSD([sQuery(id+"F0.wireOp",EDGE,"E1.0"),sQuery(id+"F0.wireOp",EDGE,"E1.1"),sQuery(id+"F0.wireOp",EDGE,"E1.2"),subQ1])],"isStart":false})]});var subQ3=makeQuery(id+"F12.imprint","INTERSECT",VERTEX,{"disambiguationData":[OD(0.0)],"derivedFrom":[subQ2,subQ0]});Q21=makeQuery(id+"F12.imprint","IMPRINT",FACE,{"disambiguationData":[TD([[makeQuery(id+"F12.imprint","IMPRINT",EDGE,{"disambiguationData":[TD([[subQ3,-1.0]])],"derivedFrom":subQ0}),1.0]])]});}
            var Q22;
            {var subQ0=sQuery(id+"F12.wireOp",EDGE,"E31.MirrorC");var subQ5=makeQuery(id+"F12.imprint","INTERSECT",VERTEX,{"derivedFrom":[sQuery(id+"F12.wireOp",EDGE,"E30.MirrorCS"),subQ0]});Q22=makeQuery(id+"F12.imprint","IMPRINT",FACE,{"disambiguationData":[TD([[makeQuery(id+"F12.imprint","IMPRINT",EDGE,{"disambiguationData":[TD([[subQ5,-1.0]])],"derivedFrom":subQ0}),1.0]])]});}
            var Q23;
            {var subQ0=sQuery(id+"F12.wireOp",EDGE,"E30.MirrorCS");Q23=makeQuery(id+"F12.imprint","IMPRINT",FACE,{"disambiguationData":[TD([[makeQuery(id+"F12.imprint","IMPRINT",EDGE,{"derivedFrom":subQ0}),1.0]])]});}
            extrude(context, id + "F21", {"entities" : qUnion([Q0, Q1, Q2, Q3, Q4, Q5, Q6, Q7, Q8, Q9, Q10, Q11, Q12, Q13, Q14, Q15, Q16, Q17, Q18, Q19, Q20, Q21, Q22, Q23]), "operationType" : NewBodyOperationType.REMOVE, "oppositeDirection" : true, "depth" : 0.7 * mm});
        }
        {
            var Q0;
            Q0=makeQuery(id+"F1.opExtrude","CAP_FACE",FACE,{"disambiguationData":[OSD([sQuery(id+"F0.wireOp",EDGE,"E0.bottom"),sQuery(id+"F0.wireOp",EDGE,"E0.top"),sQuery(id+"F0.wireOp",EDGE,"E0.left"),sQuery(id+"F0.wireOp",EDGE,"E0.right")])],"isStart":false});
            var sketch = newSketch(context, id + "F22", { "sketchPlane" : qUnion([Q0])});
            skLineSegment(sketch, "E48.bottom", {"start": v(-4.75, -11.7) * mm, "end": v(4.75, -11.7) * mm});
            skLineSegment(sketch, "E48.top", {"start": v(-4.75, -18.7) * mm, "end": v(4.75, -18.7) * mm});
            skLineSegment(sketch, "E48.left", {"start": v(-4.75, -11.7) * mm, "end": v(-4.75, -18.7) * mm});
            skLineSegment(sketch, "E48.right", {"start": v(4.75, -11.7) * mm, "end": v(4.75, -18.7) * mm});
            skLineSegment(sketch, "E49.bottom", {"start": v(-4, -12.45) * mm, "end": v(4, -12.45) * mm});
            skLineSegment(sketch, "E49.top", {"start": v(-4, -14.95) * mm, "end": v(4, -14.95) * mm});
            skLineSegment(sketch, "E49.left", {"start": v(-4, -12.45) * mm, "end": v(-4, -14.95) * mm});
            skLineSegment(sketch, "E49.right", {"start": v(4, -12.45) * mm, "end": v(4, -14.95) * mm});
            skSolve(sketch);
        }
        {
            var Q0;
            {var subQ1=sQuery(id+"F22.wireOp",EDGE,"E48.bottom");Q0=makeQuery(id+"F22.imprint","IMPRINT",FACE,{"disambiguationData":[TD([[makeQuery(id+"F22.imprint","IMPRINT",EDGE,{"derivedFrom":subQ1}),-1.0]])]});}
            var Q1;
            {var subQ0=sQuery(id+"F22.wireOp",EDGE,"E48.top");Q1=makeQuery(id+"F22.imprint","IMPRINT",FACE,{"disambiguationData":[TD([[makeQuery(id+"F22.imprint","IMPRINT",EDGE,{"derivedFrom":subQ0}),1.0]])]});}
            extrude(context, id + "F23", {"entities" : qUnion([Q0, Q1]), "operationType" : NewBodyOperationType.REMOVE, "oppositeDirection" : true, "depth" : 0.3 * mm});
        }
        {
            var Q0;
            Q0=makeQuery(id+"F23.boolean.opBoolean","COPY",EDGE,{"derivedFrom":makeQuery(id+"F23.opExtrude","SWEPT_EDGE",EDGE,{"disambiguationData":[OSD([sQuery(id+"F22.wireOp",EDGE,"E48.bottom"),sQuery(id+"F22.wireOp",EDGE,"E48.left")])]})});
            var Q1;
            Q1=makeQuery(id+"F23.boolean.opBoolean","COPY",EDGE,{"derivedFrom":makeQuery(id+"F23.opExtrude","SWEPT_EDGE",EDGE,{"disambiguationData":[OSD([sQuery(id+"F22.wireOp",EDGE,"E48.bottom"),sQuery(id+"F22.wireOp",EDGE,"E48.right")])]})});
            fillet(context, id + "F24", {"entities" : qUnion([Q0, Q1]), "radius" : 1 * mm, "tangentPropagation" : true, "allowEdgeOverflow" : false});
        }
        {
            var Q0;
            Q0=makeQuery(id+"F23.boolean.opBoolean","COPY",EDGE,{"derivedFrom":makeQuery(id+"F23.opExtrude","SWEPT_EDGE",EDGE,{"disambiguationData":[OSD([sQuery(id+"F22.wireOp",EDGE,"E49.top"),sQuery(id+"F22.wireOp",EDGE,"E49.left")])]})});
            var Q1;
            Q1=makeQuery(id+"F23.boolean.opBoolean","COPY",EDGE,{"derivedFrom":makeQuery(id+"F23.opExtrude","SWEPT_EDGE",EDGE,{"disambiguationData":[OSD([sQuery(id+"F22.wireOp",EDGE,"E49.bottom"),sQuery(id+"F22.wireOp",EDGE,"E49.left")])]})});
            var Q2;
            Q2=makeQuery(id+"F23.boolean.opBoolean","COPY",EDGE,{"derivedFrom":makeQuery(id+"F23.opExtrude","SWEPT_EDGE",EDGE,{"disambiguationData":[OSD([sQuery(id+"F22.wireOp",EDGE,"E49.top"),sQuery(id+"F22.wireOp",EDGE,"E49.right")])]})});
            var Q3;
            Q3=makeQuery(id+"F23.boolean.opBoolean","COPY",EDGE,{"derivedFrom":makeQuery(id+"F23.opExtrude","SWEPT_EDGE",EDGE,{"disambiguationData":[OSD([sQuery(id+"F22.wireOp",EDGE,"E49.bottom"),sQuery(id+"F22.wireOp",EDGE,"E49.right")])]})});
            fillet(context, id + "F25", {"entities" : qUnion([Q0, Q1, Q2, Q3]), "radius" : 0.5 * mm, "tangentPropagation" : true, "allowEdgeOverflow" : false});
        }
        {
            var Q0;
            Q0=makeQuery(id+"F23.boolean.opBoolean","COPY",EDGE,{"derivedFrom":makeQuery(id+"F23.opExtrude","CAP_EDGE",EDGE,{"disambiguationData":[OSD([sQuery(id+"F22.wireOp",EDGE,"E48.left")])],"isStart":false})});
            var Q1;
            {var subQ0=sQuery(id+"F22.wireOp",EDGE,"E48.left");var subQ1=sQuery(id+"F22.wireOp",EDGE,"E48.bottom");Q1=makeQuery(id+"F24.opFillet","BLEND_EDGE",EDGE,{"blendedFrom":[makeQuery(id+"F23.boolean.opBoolean","COPY",EDGE,{"derivedFrom":makeQuery(id+"F23.opExtrude","SWEPT_EDGE",EDGE,{"disambiguationData":[OSD([subQ1,subQ0])]})}),makeQuery(id+"F23.boolean.opBoolean","COPY",FACE,{"derivedFrom":makeQuery(id+"F23.opExtrude","CAP_FACE",FACE,{"disambiguationData":[OSD([subQ1,sQuery(id+"F22.wireOp",EDGE,"E48.top"),subQ0,sQuery(id+"F22.wireOp",EDGE,"E48.right"),sQuery(id+"F22.wireOp",EDGE,"E49.bottom"),sQuery(id+"F22.wireOp",EDGE,"E49.top"),sQuery(id+"F22.wireOp",EDGE,"E49.left"),sQuery(id+"F22.wireOp",EDGE,"E49.right")])],"isStart":false})})],"blendedInto":[makeQuery(id+"F23.boolean.opBoolean","COPY",FACE,{"derivedFrom":makeQuery(id+"F23.opExtrude","CAP_FACE",FACE,{"disambiguationData":[OSD([subQ1,sQuery(id+"F22.wireOp",EDGE,"E48.top"),subQ0,sQuery(id+"F22.wireOp",EDGE,"E48.right"),sQuery(id+"F22.wireOp",EDGE,"E49.bottom"),sQuery(id+"F22.wireOp",EDGE,"E49.top"),sQuery(id+"F22.wireOp",EDGE,"E49.left"),sQuery(id+"F22.wireOp",EDGE,"E49.right")])],"isStart":false})})]});}
            var Q2;
            Q2=makeQuery(id+"F23.boolean.opBoolean","COPY",EDGE,{"derivedFrom":makeQuery(id+"F23.opExtrude","CAP_EDGE",EDGE,{"disambiguationData":[OSD([sQuery(id+"F22.wireOp",EDGE,"E48.bottom")])],"isStart":false})});
            var Q3;
            {var subQ0=sQuery(id+"F22.wireOp",EDGE,"E48.right");var subQ1=sQuery(id+"F22.wireOp",EDGE,"E48.bottom");Q3=makeQuery(id+"F24.opFillet","BLEND_EDGE",EDGE,{"blendedFrom":[makeQuery(id+"F23.boolean.opBoolean","COPY",EDGE,{"derivedFrom":makeQuery(id+"F23.opExtrude","SWEPT_EDGE",EDGE,{"disambiguationData":[OSD([subQ1,subQ0])]})}),makeQuery(id+"F23.boolean.opBoolean","COPY",FACE,{"derivedFrom":makeQuery(id+"F23.opExtrude","CAP_FACE",FACE,{"disambiguationData":[OSD([subQ1,sQuery(id+"F22.wireOp",EDGE,"E48.top"),sQuery(id+"F22.wireOp",EDGE,"E48.left"),subQ0,sQuery(id+"F22.wireOp",EDGE,"E49.bottom"),sQuery(id+"F22.wireOp",EDGE,"E49.top"),sQuery(id+"F22.wireOp",EDGE,"E49.left"),sQuery(id+"F22.wireOp",EDGE,"E49.right")])],"isStart":false})})],"blendedInto":[makeQuery(id+"F23.boolean.opBoolean","COPY",FACE,{"derivedFrom":makeQuery(id+"F23.opExtrude","CAP_FACE",FACE,{"disambiguationData":[OSD([subQ1,sQuery(id+"F22.wireOp",EDGE,"E48.top"),sQuery(id+"F22.wireOp",EDGE,"E48.left"),subQ0,sQuery(id+"F22.wireOp",EDGE,"E49.bottom"),sQuery(id+"F22.wireOp",EDGE,"E49.top"),sQuery(id+"F22.wireOp",EDGE,"E49.left"),sQuery(id+"F22.wireOp",EDGE,"E49.right")])],"isStart":false})})]});}
            var Q4;
            Q4=makeQuery(id+"F23.boolean.opBoolean","COPY",EDGE,{"derivedFrom":makeQuery(id+"F23.opExtrude","CAP_EDGE",EDGE,{"disambiguationData":[OSD([sQuery(id+"F22.wireOp",EDGE,"E48.right")])],"isStart":false})});
            fillet(context, id + "F26", {"entities" : qUnion([Q0, Q1, Q2, Q3, Q4]), "radius" : 0.3 * mm, "tangentPropagation" : true, "allowEdgeOverflow" : false});
        }
        {
            var Q0;
            Q0=makeQuery(id+"F1.opExtrude","SWEPT_FACE",FACE,{"disambiguationData":[OSD([sQuery(id+"F0.wireOp",EDGE,"E0.left")])]});
            var sketch = newSketch(context, id + "F27", { "sketchPlane" : qUnion([Q0])});
            skLineSegment(sketch, "E50", {"start": v(2.5, 10) * mm, "end": v(2.5, -10) * mm});
            skLineSegment(sketch, "E51.bottom", {"start": v(2.5, 9.5) * mm, "end": v(5, 9.5) * mm});
            skLineSegment(sketch, "E51.top", {"start": v(2.5, 8) * mm, "end": v(5, 8) * mm});
            skLineSegment(sketch, "E51.left", {"start": v(2.5, 9.5) * mm, "end": v(2.5, 8) * mm});
            skLineSegment(sketch, "E51.right", {"start": v(5, 9.5) * mm, "end": v(5, 8) * mm});
            skLineSegment(sketch, "E52", {"start": v(2.5, 0) * mm, "end": v(35.1, 0) * mm});
            skLineSegment(sketch, "E53", {"start": v(3, 0) * mm, "end": v(3, 7.5) * mm});
            skLineSegment(sketch, "E54", {"start": v(3, 7.5) * mm, "end": v(5.5, 7.5) * mm});
            skLineSegment(sketch, "E55", {"start": v(5.5, 7.5) * mm, "end": v(5.5, 9.5) * mm});
            skLineSegment(sketch, "E56", {"start": v(5.5, 9.5) * mm, "end": v(28.6, 9.5) * mm});
            skLineSegment(sketch, "E57", {"start": v(28.6, 9.5) * mm, "end": v(28.6, 0) * mm});
            skLineSegment(sketch, "E58.MirrorCS", {"start": v(3, 0) * mm, "end": v(3, -7.5) * mm});
            skLineSegment(sketch, "E59.MirrorCS", {"start": v(3, -7.5) * mm, "end": v(5.5, -7.5) * mm});
            skLineSegment(sketch, "E60.MirrorCS", {"start": v(5.5, -7.5) * mm, "end": v(5.5, -9.5) * mm});
            skLineSegment(sketch, "E61.MirrorCS", {"start": v(5.5, -9.5) * mm, "end": v(28.6, -9.5) * mm});
            skLineSegment(sketch, "E62.MirrorCS", {"start": v(28.6, -9.5) * mm, "end": v(28.6, 0) * mm});
            skLineSegment(sketch, "E63.MirrorCS", {"start": v(2.5, -8) * mm, "end": v(5, -8) * mm});
            skLineSegment(sketch, "E64.MirrorCS", {"start": v(5, -9.5) * mm, "end": v(5, -8) * mm});
            skLineSegment(sketch, "E65.MirrorCS", {"start": v(2.5, -9.5) * mm, "end": v(5, -9.5) * mm});
            skLineSegment(sketch, "E66", {"start": v(29.1, 10) * mm, "end": v(29.1, -10) * mm});
            skLineSegment(sketch, "E67.bottom", {"start": v(29.6, 3.5) * mm, "end": v(34.6, 3.5) * mm});
            skLineSegment(sketch, "E67.top", {"start": v(29.6, -3.5) * mm, "end": v(34.6, -3.5) * mm});
            skLineSegment(sketch, "E67.left", {"start": v(29.6, 3.5) * mm, "end": v(29.6, -3.5) * mm});
            skLineSegment(sketch, "E67.right", {"start": v(34.6, 3.5) * mm, "end": v(34.6, -3.5) * mm});
            skPoint(sketch, "E67.middle", {"position": v(32.1, 0) * mm});
            skLineSegment(sketch, "E68.bottom", {"start": v(31.1, 3) * mm, "end": v(34.1, 3) * mm});
            skLineSegment(sketch, "E68.top", {"start": v(31.1, -3) * mm, "end": v(34.1, -3) * mm});
            skLineSegment(sketch, "E68.left", {"start": v(31.1, 3) * mm, "end": v(31.1, -3) * mm});
            skLineSegment(sketch, "E68.right", {"start": v(34.1, 3) * mm, "end": v(34.1, -3) * mm});
            skPoint(sketch, "E68.middle", {"position": v(32.6, 0) * mm});
            skLineSegment(sketch, "E69", {"start": v(32.1, 3) * mm, "end": v(32.1, -3) * mm});
            skLineSegment(sketch, "E70", {"start": v(31.1, -3) * mm, "end": v(31.1, -3.5) * mm});
            skLineSegment(sketch, "E71", {"start": v(31.1, 3) * mm, "end": v(31.1, 3.5) * mm});
            skSolve(sketch);
        }
        {
            var Q0;
            {var subQ10=sQuery(id+"F27.wireOp",EDGE,"E51.bottom");Q0=makeQuery(id+"F27.imprint","IMPRINT",FACE,{"disambiguationData":[TD([[makeQuery(id+"F27.imprint","IMPRINT",EDGE,{"derivedFrom":subQ10}),1.0]])]});}
            var Q1;
            {var subQ0=sQuery(id+"F27.wireOp",EDGE,"E58.MirrorCS");Q1=makeQuery(id+"F27.imprint","IMPRINT",FACE,{"disambiguationData":[TD([[makeQuery(id+"F27.imprint","IMPRINT",EDGE,{"derivedFrom":subQ0}),-1.0]])]});}
            extrude(context, id + "F28", {"entities" : qUnion([Q0, Q1]), "operationType" : NewBodyOperationType.REMOVE, "oppositeDirection" : true, "depth" : 2 * mm});
        }
        {
            var Q0;
            {var subQ0=sQuery(id+"F27.wireOp",EDGE,"E67.bottom");Q0=makeQuery(id+"F27.imprint","IMPRINT",FACE,{"disambiguationData":[TD([[makeQuery(id+"F27.imprint","IMPRINT",EDGE,{"derivedFrom":subQ0}),-1.0]])]});}
            var Q1;
            {var subQ1=sQuery(id+"F27.wireOp",EDGE,"E67.top");Q1=makeQuery(id+"F27.imprint","IMPRINT",FACE,{"disambiguationData":[TD([[makeQuery(id+"F27.imprint","IMPRINT",EDGE,{"derivedFrom":subQ1}),1.0]])]});}
            extrude(context, id + "F29", {"entities" : qUnion([Q0, Q1]), "operationType" : NewBodyOperationType.REMOVE, "oppositeDirection" : true, "depth" : 1 * mm});
        }
        {
            var Q0;
            {var subQ0=sQuery(id+"F27.wireOp",EDGE,"E71");Q0=makeQuery(id+"F27.imprint","IMPRINT",FACE,{"disambiguationData":[TD([[makeQuery(id+"F27.imprint","IMPRINT",EDGE,{"derivedFrom":subQ0}),-1.0]])]});}
            var Q1;
            {var subQ5=sQuery(id+"F27.wireOp",EDGE,"E70");Q1=makeQuery(id+"F27.imprint","IMPRINT",FACE,{"disambiguationData":[TD([[makeQuery(id+"F27.imprint","IMPRINT",EDGE,{"derivedFrom":subQ5}),1.0]])]});}
            extrude(context, id + "F30", {"entities" : qUnion([Q0, Q1]), "operationType" : NewBodyOperationType.REMOVE, "oppositeDirection" : true, "depth" : 2 * mm});
        }
        {
            var Q0;
            {var subQ0=sQuery(id+"F27.wireOp",EDGE,"E69");var subQ1=sQuery(id+"F27.wireOp",EDGE,"E52");var subQ2=makeQuery(id+"F27.imprint","INTERSECT",VERTEX,{"derivedFrom":[subQ1,subQ0]});Q0=makeQuery(id+"F27.imprint","IMPRINT",FACE,{"disambiguationData":[TD([[makeQuery(id+"F27.imprint","IMPRINT",EDGE,{"disambiguationData":[TD([[subQ2,-1.0]])],"derivedFrom":subQ1}),-1.0]])]});}
            var Q1;
            {var subQ0=sQuery(id+"F27.wireOp",EDGE,"E69");var subQ1=sQuery(id+"F27.wireOp",EDGE,"E52");var subQ2=makeQuery(id+"F27.imprint","INTERSECT",VERTEX,{"derivedFrom":[subQ1,subQ0]});Q1=makeQuery(id+"F27.imprint","IMPRINT",FACE,{"disambiguationData":[TD([[makeQuery(id+"F27.imprint","IMPRINT",EDGE,{"disambiguationData":[TD([[subQ2,-1.0]])],"derivedFrom":subQ1}),1.0]])]});}
            extrude(context, id + "F31", {"entities" : qUnion([Q0, Q1]), "operationType" : NewBodyOperationType.REMOVE, "oppositeDirection" : true, "depth" : 1.2 * mm});
        }
        {
            var Q0;
            Q0=makeQuery(id+"F29.boolean.opBoolean","COPY",EDGE,{"derivedFrom":makeQuery(id+"F29.opExtrude","SWEPT_EDGE",EDGE,{"disambiguationData":[OSD([sQuery(id+"F27.wireOp",EDGE,"E67.bottom"),sQuery(id+"F27.wireOp",EDGE,"E67.left")])]})});
            var Q1;
            Q1=makeQuery(id+"F30.boolean.opBoolean","COPY",EDGE,{"derivedFrom":makeQuery(id+"F30.opExtrude","SWEPT_EDGE",EDGE,{"disambiguationData":[OSD([sQuery(id+"F27.wireOp",EDGE,"E67.bottom"),sQuery(id+"F27.wireOp",EDGE,"E67.right")])]})});
            var Q2;
            Q2=makeQuery(id+"F30.boolean.opBoolean","COPY",EDGE,{"derivedFrom":makeQuery(id+"F30.opExtrude","SWEPT_EDGE",EDGE,{"disambiguationData":[OSD([sQuery(id+"F27.wireOp",EDGE,"E67.top"),sQuery(id+"F27.wireOp",EDGE,"E67.right")])]})});
            var Q3;
            Q3=makeQuery(id+"F29.boolean.opBoolean","COPY",EDGE,{"derivedFrom":makeQuery(id+"F29.opExtrude","SWEPT_EDGE",EDGE,{"disambiguationData":[OSD([sQuery(id+"F27.wireOp",EDGE,"E67.top"),sQuery(id+"F27.wireOp",EDGE,"E67.left")])]})});
            fillet(context, id + "F32", {"entities" : qUnion([Q0, Q1, Q2, Q3]), "radius" : 1 * mm, "tangentPropagation" : true, "allowEdgeOverflow" : false});
        }
        {
            var Q0;
            Q0=makeQuery(id+"F31.boolean.opBoolean","COPY",EDGE,{"derivedFrom":makeQuery(id+"F31.opExtrude","SWEPT_EDGE",EDGE,{"disambiguationData":[OSD([sQuery(id+"F27.wireOp",EDGE,"E68.bottom"),sQuery(id+"F27.wireOp",EDGE,"E69")])]})});
            var Q1;
            Q1=makeQuery(id+"F31.boolean.opBoolean","COPY",EDGE,{"derivedFrom":makeQuery(id+"F31.opExtrude","SWEPT_EDGE",EDGE,{"disambiguationData":[OSD([sQuery(id+"F27.wireOp",EDGE,"E68.top"),sQuery(id+"F27.wireOp",EDGE,"E69")])]})});
            var Q2;
            {var subQ0=sQuery(id+"F27.wireOp",EDGE,"E68.top");var subQ2=sQuery(id+"F27.wireOp",EDGE,"E70");var subQ3=sQuery(id+"F27.wireOp",EDGE,"E68.left");Q2=makeQuery(id+"F30.boolean.opBoolean","COPY",EDGE,{"disambiguationData":[TD([makeQuery(id+"F1.opExtrude","SWEPT_FACE",FACE,{"disambiguationData":[OSD([sQuery(id+"F0.wireOp",EDGE,"E0.left")])]})])],"derivedFrom":makeQuery(id+"F30.opExtrude","SWEPT_EDGE",EDGE,{"disambiguationData":[OSD([subQ0,subQ3,subQ2])]})});}
            var Q3;
            {var subQ0=sQuery(id+"F27.wireOp",EDGE,"E68.bottom");var subQ1=sQuery(id+"F27.wireOp",EDGE,"E71");var subQ3=sQuery(id+"F27.wireOp",EDGE,"E68.left");Q3=makeQuery(id+"F30.boolean.opBoolean","COPY",EDGE,{"disambiguationData":[TD([makeQuery(id+"F1.opExtrude","SWEPT_FACE",FACE,{"disambiguationData":[OSD([sQuery(id+"F0.wireOp",EDGE,"E0.left")])]})])],"derivedFrom":makeQuery(id+"F30.opExtrude","SWEPT_EDGE",EDGE,{"disambiguationData":[OSD([subQ0,subQ3,subQ1])]})});}
            fillet(context, id + "F33", {"entities" : qUnion([Q0, Q1, Q2, Q3]), "radius" : 0.3 * mm, "tangentPropagation" : true, "allowEdgeOverflow" : false});
        }
        {
            var Q0;
            Q0=makeQuery(id+"F31.boolean.opBoolean","COPY",EDGE,{"derivedFrom":makeQuery(id+"F31.opExtrude","CAP_EDGE",EDGE,{"disambiguationData":[OSD([sQuery(id+"F27.wireOp",EDGE,"E69")])],"isStart":false})});
            fillet(context, id + "F34", {"entities" : qUnion([Q0]), "radius" : 1.5 * mm, "tangentPropagation" : true, "allowEdgeOverflow" : false});
        }
        {
            var Q0;
            Q0=makeQuery(id+"F29.boolean.opBoolean","COPY",EDGE,{"derivedFrom":makeQuery(id+"F29.opExtrude","CAP_EDGE",EDGE,{"disambiguationData":[OSD([sQuery(id+"F27.wireOp",EDGE,"E67.left")])],"isStart":false})});
            fillet(context, id + "F35", {"entities" : qUnion([Q0]), "radius" : 1 * mm, "tangentPropagation" : true, "allowEdgeOverflow" : false});
        }
    });
